# Revit family: РИДАН_RJIP Premium FB_WW_H DN15-125
name_source: partatom
category: Арматура трубопроводов
units: mm (PartAtom-declared; Revit-internal decimal feet)

## family parameters
Всегда вертикально = Да
На основе рабочей плоскости = Нет
Общий = Нет
При загрузке вырезать с полостями = Нет
Размер круглого соединителя = Использовать диаметр
Тип детали = Вставляется

## types (10) — shared parameters
ADSK_Версия Revit = 2019
ADSK_Версия семейства = 1.0
ADSK_Единица измерения = шт.
ADSK_Завод-изготовитель = ООО «Ридан-Трейд»
ADSK_Количество = 1
ADSK_Потеря давления жидкости = 0.0 Па
ADSK_Расход жидкости = 0 м³/ч
LT = Table
URL = https://ridan.ru
Изготовитель = ООО «Ридан-Трейд»

## per-type parameters (varying)
| type | ADSK_Диаметр условный | ADSK_Код изделия | ADSK_Марка | ADSK_Масса | ADSK_Наименование | ADSK_Пропускная способность | a | b | c | d | e | f | g | h | i |
| DN 15 | 15 мм | 065N1100R | RJIP Premium FB WW DN15 PN40 H | 1.5 | RJIP Premium Кран шаровой FB WW DN15 PN40 H (приварной, с рукояткой, полнопроходной) | 18 м³/ч | 41 мм | 12 мм | 100 мм | 50 мм | 21 мм | 42 мм | 73 мм | 27 мм | 205 мм |
| DN 20 | 20 мм | 065N1105R | RJIP Premium FB WW DN20 PN40 H | 1.4 | RJIP Premium Кран шаровой FB WW DN20 PN40 H (приварной, с рукояткой, полнопроходной) | 46 м³/ч | 65 мм | 15 мм | 70 мм | 35 мм | 34 мм | 42 мм | 76 мм | 27 мм | 230 мм |
| DN 25 | 25 мм | 065N1110R | RJIP Premium FB WW DN25 PN40 H | 1.75 | RJIP Premium Кран шаровой FB WW DN25 PN40 H (приварной, с рукояткой, полнопроходной) | 71 м³/ч | 80 мм | 19 мм | 62 мм | 31 мм | 42 мм | 57 мм | 81 мм | 27 мм | 260 мм |
| DN 32 | 32 мм | 065N1115R | RJIP Premium FB WW DN32 PN40 H | 4.05 | RJIP Premium Кран шаровой FB WW DN32 PN40 H (приварной, с рукояткой, полнопроходной) | 79 м³/ч | 90 мм | 25 мм | 70 мм | 35 мм | 48 мм | 76 мм | 87 мм | 34 мм | 300 мм |
| DN 40 | 40 мм | 065N1120R | RJIP Premium FB WW DN40 PN40 H | 5 | RJIP Premium Кран шаровой FB WW DN40 PN40 H (приварной, с рукояткой, полнопроходной) | 125 м³/ч | 81 мм | 25 мм | 87 мм | 44 мм | 57 мм | 89 мм | 93 мм | 34 мм | 300 мм |
| DN 50 | 50 мм | 065N1125R | RJIP Premium FB WW DN50 PN40 H | 6.5 | RJIP Premium Кран шаровой FB WW DN50 PN40 H (приварной, с рукояткой, полнопроходной) | 189 м³/ч | 44 мм | 46 мм | 120 мм | 60 мм | 60 мм | 114 мм | 108 мм | 34 мм | 300 мм |
| DN 65 | 65 мм | 065N1130R | RJIP Premium FB WW DN65 PN25 H | 9 | RJIP Premium Кран шаровой FB WW DN65 PN25 H (приварной, с рукояткой, полнопроходной) | 328 м³/ч | 39 мм | 36 мм | 150 мм | 75 мм | 76 мм | 140 мм | 124 мм | 39 мм | 300 мм |
| DN 80 | 80 мм | 065N1135R | RJIP Premium FB WW DN80 PN25 H | 12.5 | RJIP Premium Кран шаровой FB WW DN80 PN25 H (приварной, с рукояткой, полнопроходной) | 494 м³/ч | 33 мм | 50 мм | 160 мм | 80 мм | 89 мм | 159 мм | 136 мм | 39 мм | 325 мм |
| DN 100 | 100 мм | 065N1740R | RJIP Premium FB WW DN100 PN25 H | 13.83 | RJIP Premium Кран шаровой FB WW DN100 PN25 H (приварной, с рукояткой, полнопроходной) | 1358 м³/ч | 25 мм | 44 мм | 183 мм | 92 мм | 108 мм | 180 мм | 150 мм | 49 мм | 320 мм |
| DN 125 | 125 мм | 065N1745R | RJIP Premium FB WW DN125 PN25 H | 25 | RJIP Premium Кран шаровой FB WW DN125 PN25 H (приварной, с рукояткой, полнопроходной) | 2156 м³/ч | 36 мм | 29 мм | 220 мм | 110 мм | 133 мм | 219 мм | 172 мм | 49 мм | 350 мм |
